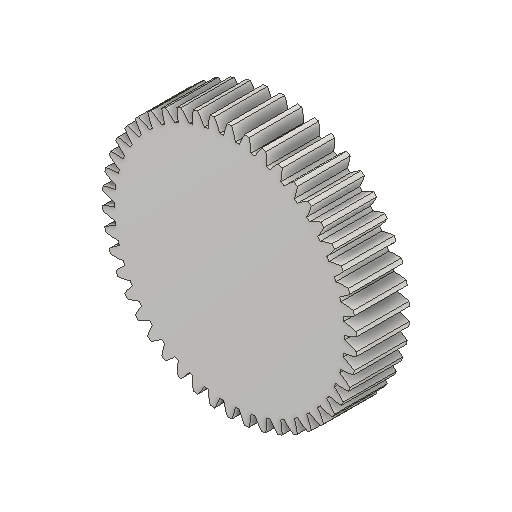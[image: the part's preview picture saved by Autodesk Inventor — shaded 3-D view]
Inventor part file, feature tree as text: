
AUTODESK INVENTOR PART (.ipt)
format: ipt  version: 2024 (Build 280153000, 153)  size: 331,776 bytes
history: native  units: mm (DEFAULTED — no unit token found)
features: plane x3, other x3, extrude x1, sketch x1
ambient origin geometry x8: Origin, YZ Plane, XZ Plane, XY Plane, X Axis, Y Axis, Z Axis, Center Point
bodies: Solid1 (feature_tree)
feature tree (8):
  extrude  "Extrusion1"  Depth=20.0mm TaperAngle=0.0deg
  plane  "Work Plane2"
  plane  "Work Plane8"
  plane  "Work Plane9"
  other  "Spur Gear"
  sketch  "Sketch1"  dims[d0=96.0mm d1=20.0mm d2=0.0mm d3=92.0mm d4=10.0mm d5=0.0mm d16=160.0mm d17=0.0mm d34=0.682955mm d39=0.0mm d41=0.0mm d43=160.0mm d46=160.0mm d47=0.0mm d48=0.0mm]
  other  "Srf1"
  other  "Pitch Diameter"
